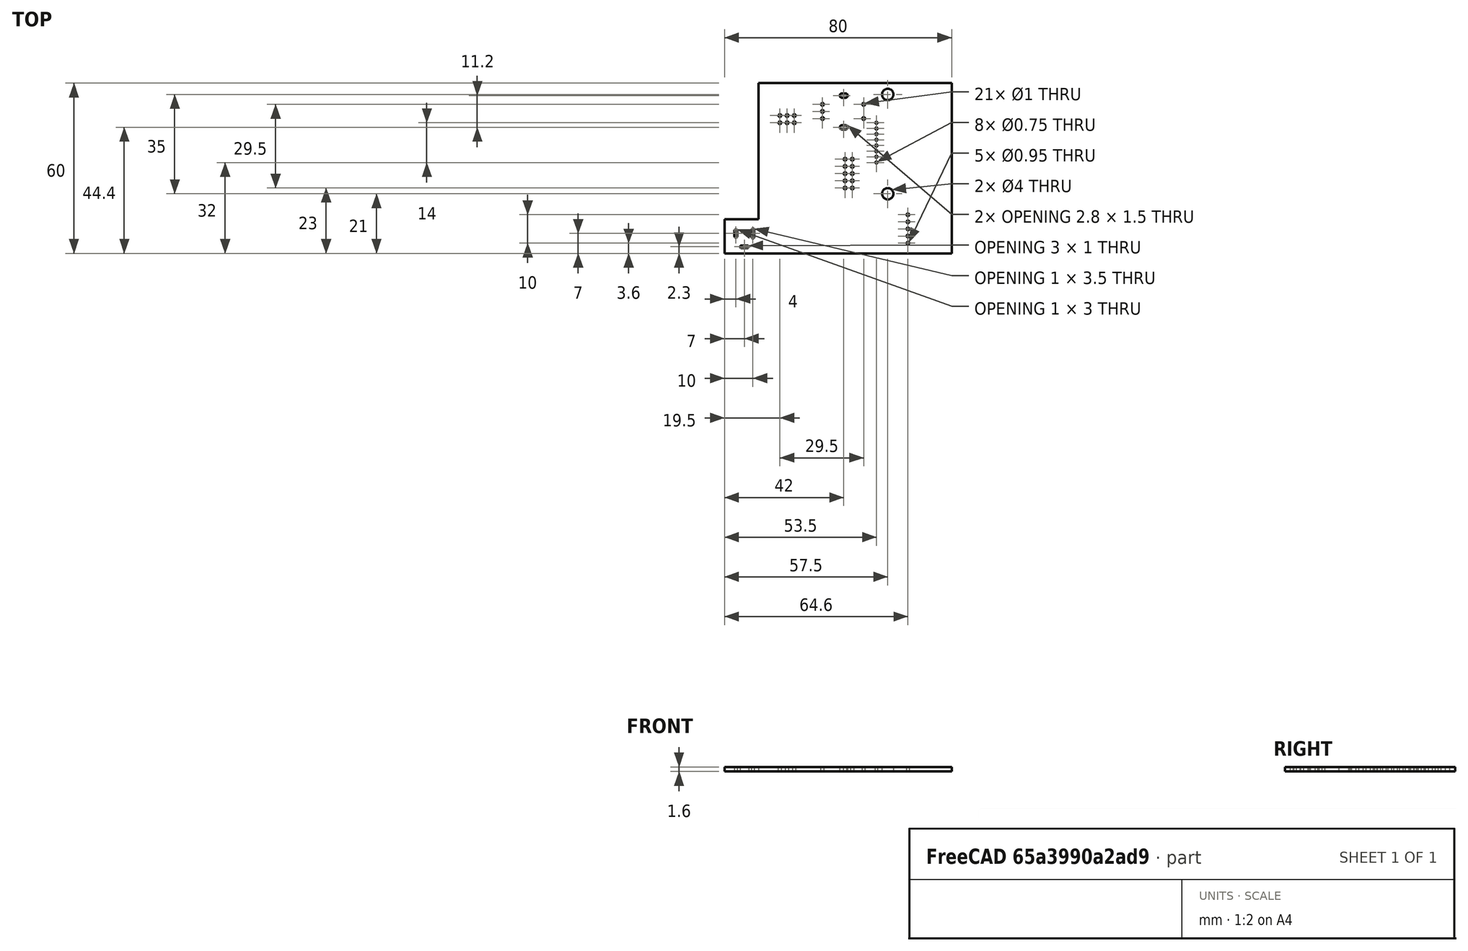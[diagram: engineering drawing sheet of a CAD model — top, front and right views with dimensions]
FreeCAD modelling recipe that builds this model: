
FCSTD DOCUMENT  (FreeCAD 0.19R24291 (Git))
Label: PCB_outline
License: All rights reserved
LicenseURL: http://en.wikipedia.org/wiki/All_rights_reserved
objects: App::Part×2, Sketcher::SketchObject×1, PartDesign::CoordinateSystem×1, Part::Feature×1
note: 3 computed .brp shape members not serialized (recipe doc carries the construction recipe); baked Part::Feature solids carry a one-line shape summary decoded from their .brp
EXTERNAL_REF file=data.FCStd obj=Spreadsheet

FEATURE [Sketcher::SketchObject] PCB_Sketch_18fc
  FullyConstrained = true
  MapMode = 5
  Support = -> [XY_Plane]
  expr: Constraints[13] = data#<<data>>.PCBLength
  expr: Constraints[14] = data#<<data>>.PCBWidth
  expr: Constraints[19] = data#<<data>>.Gear02Dist
  expr: Constraints[9] = data#<<data>>.StepperMountDiameter
  expr: Constraints[18] = data#<<data>>.M3DiameterHole
  expr: Constraints[15] = data#<<data>>.StepperMountDiameter / 2 + 2mm
  expr: Constraints[8] = data#<<data>>.StepperMountWidth
  expr: Constraints[29] = data#<<data>>.PCBGear02X
  sketch-geometry (11):
    g0: LineSegment StartX=60 StartY=100 StartZ=0 EndX=60 EndY=0 EndZ=0
    g1: LineSegment StartX=60 StartY=0 StartZ=0 EndX=0 EndY=0 EndZ=0
    g2: LineSegment StartX=0 StartY=100 StartZ=0 EndX=60 EndY=100 EndZ=0
    g3: LineSegment StartX=0 StartY=100 StartZ=0 EndX=0 EndY=0 EndZ=0
    g4: Circle CenterX=25.8 CenterY=95.8 CenterZ=0 NormalX=0 NormalY=0 NormalZ=1 AngleXU=0 Radius=2.2
    g5: Circle CenterX=25.8 CenterY=60.8 CenterZ=0 NormalX=0 NormalY=0 NormalZ=1 AngleXU=0 Radius=2.2
    g6: LineSegment StartX=25.8 StartY=95.8 StartZ=0 EndX=25.8 EndY=60.8 EndZ=0
    g7: LineSegment StartX=25.8 StartY=78.3 StartZ=0 EndX=56.3 EndY=78.3 EndZ=0
    g8: Circle CenterX=56.3 CenterY=78.3 CenterZ=0 NormalX=0 NormalY=0 NormalZ=1 AngleXU=0 Radius=1.7
    g9: Circle CenterX=55 CenterY=5 CenterZ=0 NormalX=0 NormalY=0 NormalZ=1 AngleXU=0 Radius=1.7
    g10: Circle CenterX=16 CenterY=5 CenterZ=0 NormalX=0 NormalY=0 NormalZ=1 AngleXU=0 Radius=1.7
  constraints (30):
    c: Coincident(g1,g0)
    c: Horizontal(g1)
    c: Vertical(g0)
    c: Horizontal(g2)
    c: Vertical(g3)
    c: Coincident(g2,g3)
    c: Vertical(g4,g5)
    c: Equal(g4,g5)
    c: DistanceY(g5,g4) = 35
    c: Diameter(g4) = 4.4
    c: Coincident(g6,g4)
    c: Coincident(g6,g5)
    c: Coincident(g0,g2)
    c: DistanceY(g0,g0) = 100
    c: DistanceX(g1,g1) = 60
    c: DistanceY(g4,g0) = 4.2
    c: Horizontal(g7)
    c: Coincident(g8,g7)
    c: Diameter(g8) = 3.4
    c: DistanceX(g7,g7) = 30.5
    c: Symmetric(g4,g5,g7)
    c: Coincident(g1,g-1)
    c: Coincident(g3,g1)
    c: Horizontal(g10,g9)
    c: Equal(g8,g9)
    c: Equal(g9,g10)
    c: DistanceY(g0,g9) = 5
    c: DistanceX(g9,g0) = 5
    c: DistanceX(g1,g10) = 16
    c: DistanceX(g8,g0) = 3.7
FEATURE [PartDesign::CoordinateSystem] Local_CS_18fc
  AttacherType = Attacher::AttachEngine3D
FEATURE [Part::Feature] Pcb_18fc
  Placement = pos=(-92.71,154.78,0) rot=(0,0,1;0rad)
  shape: bbox 80 x 60 x 1.6 mm, 74 faces (baked)
FEATURE [App::Part] Board_Geoms_18fc
  Group = -> [Local_CS_18fc,Pcb_18fc,PCB_Sketch_18fc]
  Origin = -> Origin
FEATURE [App::Part] Board_18fc  label="TeaSteaper"
  Group = -> [Board_Geoms_18fc]
  Origin = -> Origin001
